# Revit family: FERNHURST 20W Post Top Light, Black, Non-Dim, 3000K
name_source: partatom
category: Lighting Fixtures
units: mm (PartAtom-declared; Revit-internal decimal feet)

## family parameters
Always vertical = Yes
Cut with Voids When Loaded = No
Light Source = Yes
Part Type = Normal
Room Calculation Point = No
Round Connector Dimension = Use Diameter
Shared = No
Work Plane-Based = No

## types (1)
- FERNHURST 20W Post Top Light, Black, Non-Dim, 3000K
    Color Filter = 16777215
    Default Elevation = 0 mm  [stored 0 ft]
    Dimming Lamp Color Temperature Shift = <None>
    Emit Shape Visible in Rendering = No
    Emit from Circle Diameter = 610 mm
    Manufacturer = Decrolux
    Model = FERNHURST 20W
    Photometric Web File = IES-LC3181-FERNHURST-20W-4000K.IES
    Spigot Size = 90mm (Dia)
    Tilt Angle = 90.00°
    Type Comments = Modern Post Top Light
    Wattage Comments = 20W

note: [stored X ft] marks values corroborated as IEEE doubles in the binary element streams (Revit-internal decimal feet)

## geometry (parser evidence)
native form markers: Sweep x2
no freeform markers — native parametric forms only
